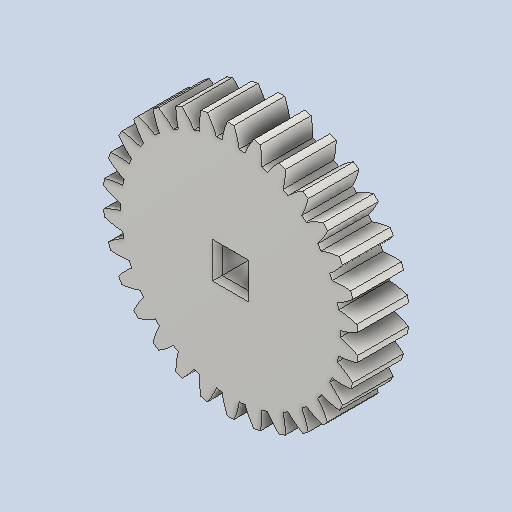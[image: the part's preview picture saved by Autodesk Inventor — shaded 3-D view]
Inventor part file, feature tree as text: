
AUTODESK INVENTOR PART (.ipt)
format: ipt  version: 2022 (Build 260153000, 153)  size: 338,944 bytes
history: native  units: in
note: dims shown in document units (in); Inventor stores cm internally (conversion verified against a paired STEP export)
features: other x12, sketch x3, plane x3
ambient origin geometry x8: Origin, YZ Plane, XZ Plane, XY Plane, X Axis, Y Axis, Z Axis, Center Point
bodies: Solid1 (feature_tree)
feature tree (18):
  other  "Spur Gear1"
  other  "Solid1::Spur Gear1"
  other  "TaggingFeature1"
  sketch  "Sketch1"  dims[d0=0.3937in]
  sketch  "Sketch2"  dims[d9=0.0in]
  sketch  "Sketch3"  dims[d14=0.0in d15=1.0in d16=0.0in d17=0.0in d18=0.0in d19=1.0in]
  plane  "XZ Plane_1"
  plane  "Work Plane2"
  plane  "Work Plane3"
  other  "Srf1"
  other  "Srf1::Derived"
  other  "Start plane iMate"
  other  "Distance iMate"
  other  "Position iMate"
  other  "Mesh iMate"
  other  "Axis iMate"
  other  "Mesh iMate2"
  other  "Align iMate"
